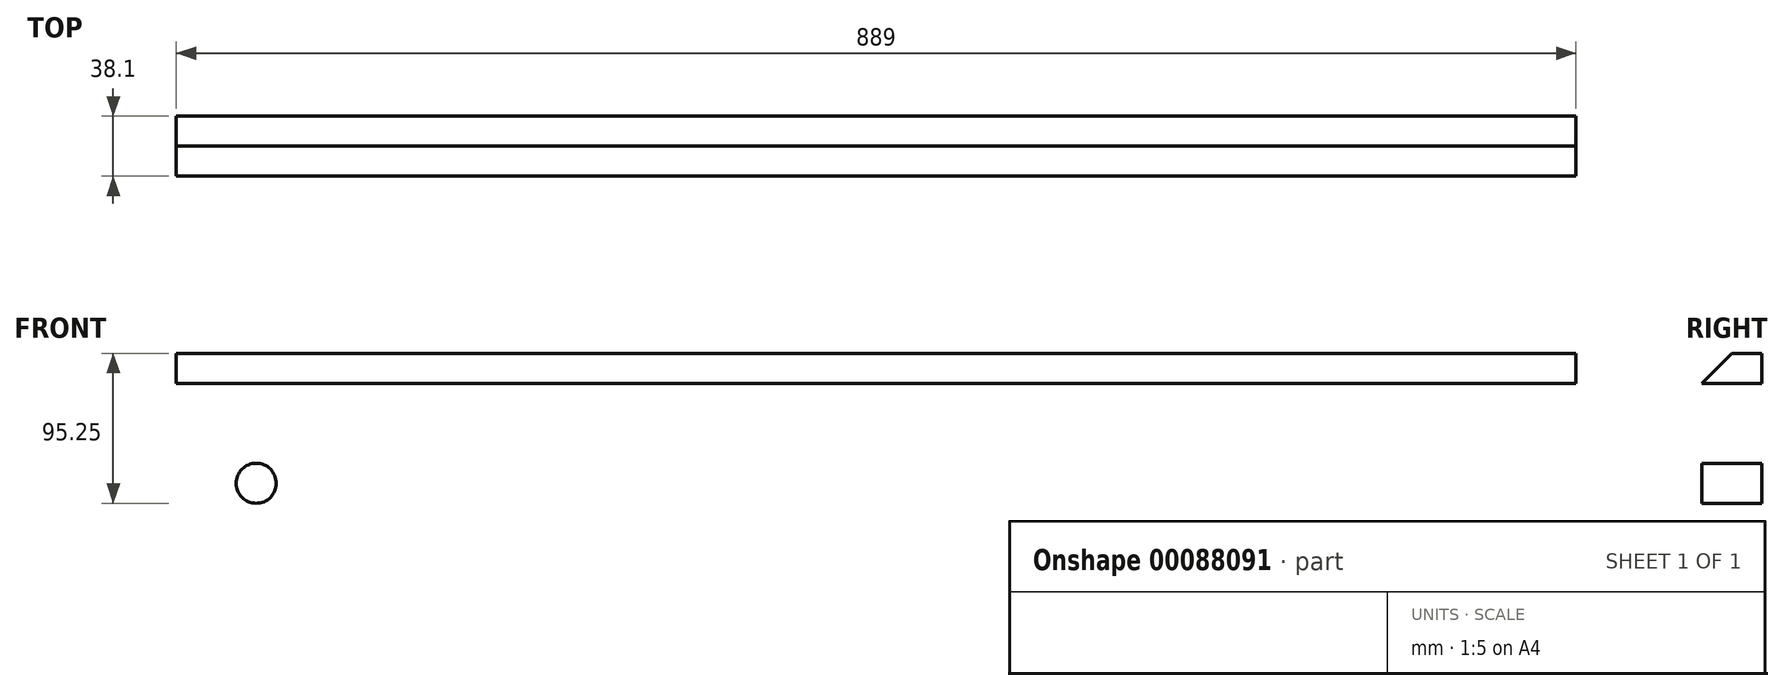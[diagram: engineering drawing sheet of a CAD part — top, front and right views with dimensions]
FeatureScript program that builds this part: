
annotation { "Feature Type Name" : "Feature", "Feature Type Description" : "" }
export const myFeature = defineFeature(function(context is Context, id is Id, definition is map)
    precondition{}
    {
        {
            var Q0;
            Q0=qCreatedBy(makeId("Right.planeOp"),FACE);
            var sketch = newSketch(context, id + "F0", { "sketchPlane" : qUnion([Q0])});
            skLineSegment(sketch, "E0.bottom", {"start": v(-19.05, 69.85) * mm, "end": v(0, 69.85) * mm});
            skLineSegment(sketch, "E0.top", {"start": v(-19.05, -69.85) * mm, "end": v(0, -69.85) * mm});
            skLineSegment(sketch, "E0.left", {"start": v(-19.05, 69.85) * mm, "end": v(-19.05, -69.85) * mm});
            skLineSegment(sketch, "E0.right", {"start": v(0, 69.85) * mm, "end": v(0, -69.85) * mm});
            skLineSegment(sketch, "E1.bottom", {"start": v(0, 69.85) * mm, "end": v(19.05, 69.85) * mm});
            skLineSegment(sketch, "E1.top", {"start": v(0, -69.85) * mm, "end": v(19.05, -69.85) * mm});
            skLineSegment(sketch, "E1.right", {"start": v(19.05, 69.85) * mm, "end": v(19.05, -69.85) * mm});
            skSolve(sketch);
        }
        {
            var Q0;
            Q0=makeQuery(id+"F0.imprint","IMPRINT",FACE,{"disambiguationData":[TD([[makeQuery(id+"F0.imprint","IMPRINT",EDGE,{"derivedFrom":sQuery(id+"F0.wireOp",EDGE,"E0.bottom")}),-1.0]])]});
            var Q1;
            Q1=makeQuery(id+"F0.imprint","IMPRINT",FACE,{"disambiguationData":[TD([[makeQuery(id+"F0.imprint","IMPRINT",EDGE,{"derivedFrom":sQuery(id+"F0.wireOp",EDGE,"E1.bottom")}),-1.0]])]});
            extrude(context, id + "F1", {"entities" : qUnion([Q0, Q1]), "endBound" : BoundingType.SYMMETRIC, "depth" : 889 * mm});
        }
        {
            var Q0;
            Q0=makeQuery(id+"F1.opExtrude","SWEPT_EDGE",EDGE,{"disambiguationData":[OSD([sQuery(id+"F0.wireOp",EDGE,"E0.bottom"),sQuery(id+"F0.wireOp",EDGE,"E0.left")])]});
            chamfer(context, id + "F2", {"entities" : qUnion([Q0]), "width" : 19.05 * mm, "tangentPropagation" : true});
        }
        {
            var Q0;
            Q0=makeQuery(id+"F1.opExtrude","SWEPT_FACE",FACE,{"disambiguationData":[OSD([sQuery(id+"F0.wireOp",EDGE,"E0.left")])]});
            var sketch = newSketch(context, id + "F3", { "sketchPlane" : qUnion([Q0])});
            skLineSegment(sketch, "E2.0", {"start": v(-444.5, 69.85) * mm, "end": v(444.5, 69.85) * mm});
            skLineSegment(sketch, "E3.0", {"start": v(444.5, 50.8) * mm, "end": v(444.5, -69.85) * mm});
            skLineSegment(sketch, "E4", {"start": v(338.95, 0) * mm, "end": v(444.5, 0) * mm, "construction": true});
            skLineSegment(sketch, "E5", {"start": v(337.87, -6.35) * mm, "end": v(444.5, -6.35) * mm, "construction": true});
            skLineSegment(sketch, "E6", {"start": v(338.23, -12.7) * mm, "end": v(444.5, -12.7) * mm, "construction": true});
            skLineSegment(sketch, "E7", {"start": v(393.7, 69.85) * mm, "end": v(393.7, -69.85) * mm, "construction": true});
            skCircle(sketch, "E8", {"center": v(393.7, -12.7) * mm, "radius": 12.7 * mm});
            skLineSegment(sketch, "E9", {"start": v(0, 69.85) * mm, "end": v(0, -69.85) * mm, "construction": true});
            skCircle(sketch, "E10.MirrorC", {"center": v(-393.7, -12.7) * mm, "radius": 12.7 * mm});
            skSolve(sketch);
        }
        {
            var Q0;
            Q0=makeQuery(id+"F3.imprint","IMPRINT",FACE,{"disambiguationData":[TD([[makeQuery(id+"F3.imprint","IMPRINT",EDGE,{"derivedFrom":sQuery(id+"F3.wireOp",EDGE,"E10.MirrorC")}),-1.0]])]});
            var Q1;
            Q1=makeQuery(id+"F3.imprint","IMPRINT",FACE,{"disambiguationData":[TD([[makeQuery(id+"F3.imprint","IMPRINT",EDGE,{"derivedFrom":sQuery(id+"F3.wireOp",EDGE,"E8")}),1.0]])]});
            extrude(context, id + "F4", {"entities" : qUnion([Q0, Q1]), "operationType" : NewBodyOperationType.REMOVE, "endBound" : BoundingType.THROUGH_ALL, "oppositeDirection" : true, "depth" : 25.4 * mm});
        }
    });
